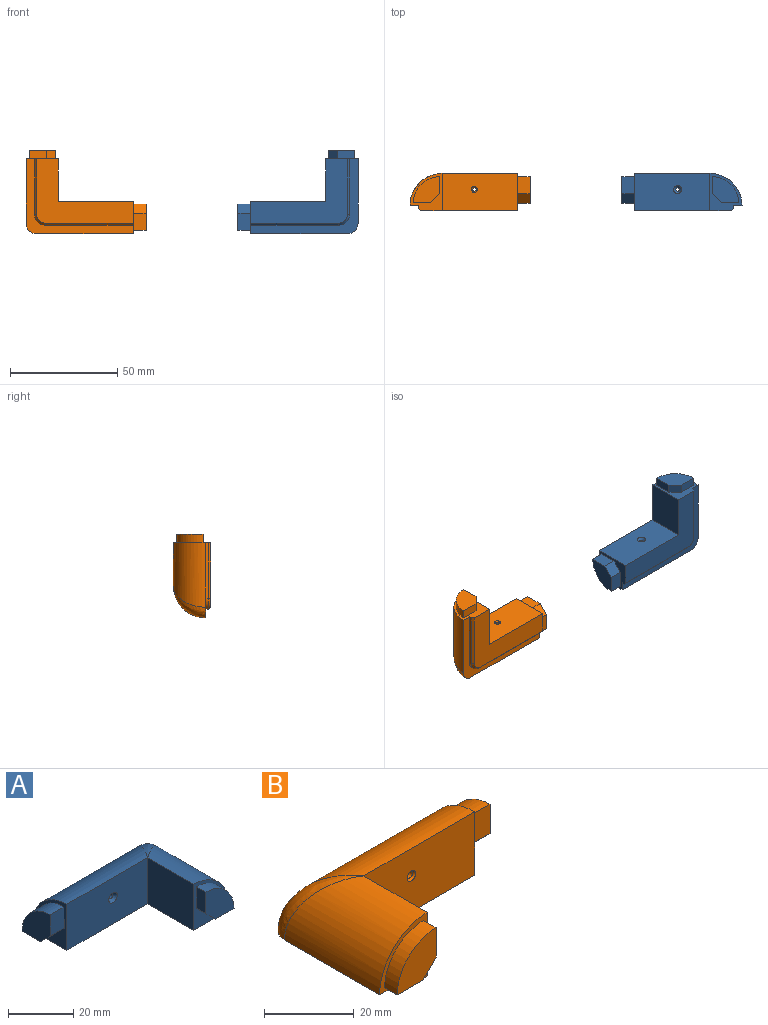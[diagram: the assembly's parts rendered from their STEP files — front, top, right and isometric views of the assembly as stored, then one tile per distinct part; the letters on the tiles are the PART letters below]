
ASSEMBLY  parts=2 mates=3
PART A: 27 faces, bbox 56x39x17.6 mm
  f0: plane 50x35mm, normal (0,0,-1), area 324mm2, adj f1,f4,f16,f17,f18,f19,f20,f22
  f1: plane 17.3x15mm, normal (-1,0,0), area 92.8mm2, adj f0,f2,f6,f7,f8,f9,f18,f19
  f2: plane 35x17.3mm, normal (0,-1,0), area 594.7mm2, adj f1,f3,f18,f21,f26
  f3: plane 20x17.3mm, normal (-1,0,0), area 346mm2, adj f2,f4,f16,f21
  f4: plane 17.3x15mm, normal (0,-1,0), area 92.8mm2, adj f0,f3,f11,f12,f13,f14,f16,f20
  f5: cylinder r=0.85mm len=12.45mm, axis (0,-1,0), area 63.9mm2, adj f18,f26
  f6: cylinder r=12.24mm len=12.24mm, axis (1,0,0), area 115.4mm2, adj f1,f7,f9,f10
  f7: plane 8x6mm, normal (0,0,-1), area 48mm2, adj f1,f6,f8,f10
  f8: plane 6x4.24mm, normal (0,-0.71,-0.71), area 36mm2, adj f1,f7,f9,f10
  f9: plane 8x6mm, normal (0,-1,0), area 48mm2, adj f1,f6,f8,f10
  f10: plane 12.24x12.24mm, normal (-1,0,0), area 108.7mm2, adj f6,f7,f8,f9
  f11: plane 8x4mm, normal (-1,0,0), area 32mm2, adj f4,f12,f14,f15
  f12: plane 4.24x4.24mm, normal (-0.71,0,-0.71), area 24mm2, adj f4,f11,f13,f15
  f13: plane 8x4mm, normal (0,0,-1), area 32mm2, adj f4,f12,f14,f15
  f14: cylinder r=12.24mm len=12.24mm, axis (0,1,0), area 76.9mm2, adj f4,f11,f13,f15
  f15: plane 12.24x12.24mm, normal (0,-1,0), area 108.7mm2, adj f11,f12,f13,f14
  f16: cylinder r=15mm len=30mm, axis (0,-1,0), area 621.2mm2, adj f0,f3,f4,f17
  f17: bspline ~17.59x15mm, area 125.7mm2, adj f0,f16,f18
  f18: cylinder r=15mm len=45mm, axis (1,0,0), area 972mm2, adj f0,f1,f2,f5,f17
  f19: plane 41x1.3mm, normal (0,1,0), area 53.3mm2, adj f0,f1,f22,f25
  f20: plane 26x1.3mm, normal (1,0,0), area 33.8mm2, adj f0,f4,f22,f23
  f21: plane 45x30mm, normal (0,0,-1), area 646.6mm2, adj f1,f2,f3,f4,f23,f24,f25
  f22: cylinder r=5mm len=5mm, axis (0,0,1), area 10.2mm2, adj f0,f19,f20,f24
  f23: plane 26x1mm, normal (0.71,0,-0.71), area 36.8mm2, adj f4,f20,f21,f24
  f24: cone r=4mm half-angle=45deg, axis (0,0,1), area 10mm2, adj f21,f22,f23,f25
  f25: plane 41x1mm, normal (0,0.71,-0.71), area 58mm2, adj f1,f19,f21,f24
  f26: cone r=0.85mm half-angle=45deg, axis (0,-1,0), area 12mm2, adj f2,f5
PART B: 27 faces, bbox 56x39x17.6 mm
  f0: plane 50x35mm, normal (0,0,-1), area 324mm2, adj f1,f2,f16,f17,f18,f20,f21,f23
  f1: plane 17.3x15mm, normal (1,0,0), area 92.8mm2, adj f0,f4,f11,f12,f13,f14,f18,f21
  f2: plane 17.3x15mm, normal (0,-1,0), area 92.8mm2, adj f0,f3,f6,f7,f8,f9,f16,f20
  f3: plane 20x17.3mm, normal (1,0,0), area 346mm2, adj f2,f4,f16,f22
  f4: plane 35x17.3mm, normal (0,-1,0), area 599.8mm2, adj f1,f3,f18,f19,f22
  f5: cylinder r=0.85mm len=12.95mm, axis (0,-1,0), area 66.6mm2, adj f18,f19
  f6: cylinder r=12.24mm len=12.24mm, axis (0,1,0), area 76.9mm2, adj f2,f7,f9,f10
  f7: plane 8x4mm, normal (0,0,-1), area 32mm2, adj f2,f6,f8,f10
  f8: plane 4.24x4.24mm, normal (0.71,0,-0.71), area 24mm2, adj f2,f7,f9,f10
  f9: plane 8x4mm, normal (1,0,0), area 32mm2, adj f2,f6,f8,f10
  f10: plane 12.24x12.24mm, normal (0,-1,0), area 108.7mm2, adj f6,f7,f8,f9
  f11: plane 8x6mm, normal (0,0,-1), area 48mm2, adj f1,f12,f14,f15
  f12: cylinder r=12.24mm len=12.24mm, axis (-1,0,0), area 115.4mm2, adj f1,f11,f13,f15
  f13: plane 8x6mm, normal (0,-1,0), area 48mm2, adj f1,f12,f14,f15
  f14: plane 6x4.24mm, normal (0,-0.71,-0.71), area 36mm2, adj f1,f11,f13,f15
  f15: plane 12.24x12.24mm, normal (1,0,0), area 108.7mm2, adj f11,f12,f13,f14
  f16: cylinder r=15mm len=30mm, axis (0,1,0), area 621.2mm2, adj f0,f2,f3,f17
  f17: bspline ~17.59x15mm, area 125.8mm2, adj f0,f16,f18
  f18: cylinder r=15mm len=45mm, axis (1,0,0), area 972mm2, adj f0,f1,f4,f5,f17
  f19: cone r=0.85mm half-angle=45deg, axis (0,-1,0), area 4.9mm2, adj f4,f5
  f20: plane 26x1.3mm, normal (-1,0,0), area 33.8mm2, adj f0,f2,f23,f24
  f21: plane 41x1.3mm, normal (0,1,0), area 53.3mm2, adj f0,f1,f23,f26
  f22: plane 45x30mm, normal (0,0,-1), area 646.6mm2, adj f1,f2,f3,f4,f24,f25,f26
  f23: cylinder r=5mm len=5mm, axis (0,0,1), area 10.2mm2, adj f0,f20,f21,f25
  f24: plane 26x1mm, normal (-0.71,0,-0.71), area 36.8mm2, adj f2,f20,f22,f25
  f25: cone r=4mm half-angle=45deg, axis (0,0,1), area 10mm2, adj f22,f23,f24,f26
  f26: plane 41x1mm, normal (0,0.71,-0.71), area 58mm2, adj f1,f21,f22,f25
PLACE A rot(axis=(-1,0,0),90deg) t=(17.55,-6.33,0)mm
PLACE B rot(axis=(-1,0,0),90deg) t=(-107.18,-6.33,0)mm
MATE revolute B.f18 <-> A.f18  axis (1,0,0) through (-94.82,-6.33,0)mm
MATE parallel B.f4 <-> A.f2  axis (0,0,1) through (-89.66,0.01,0)mm
MATE parallel B.f22 <-> A.f21  axis (0,-1,0) through (-89.68,-8.63,0)mm
